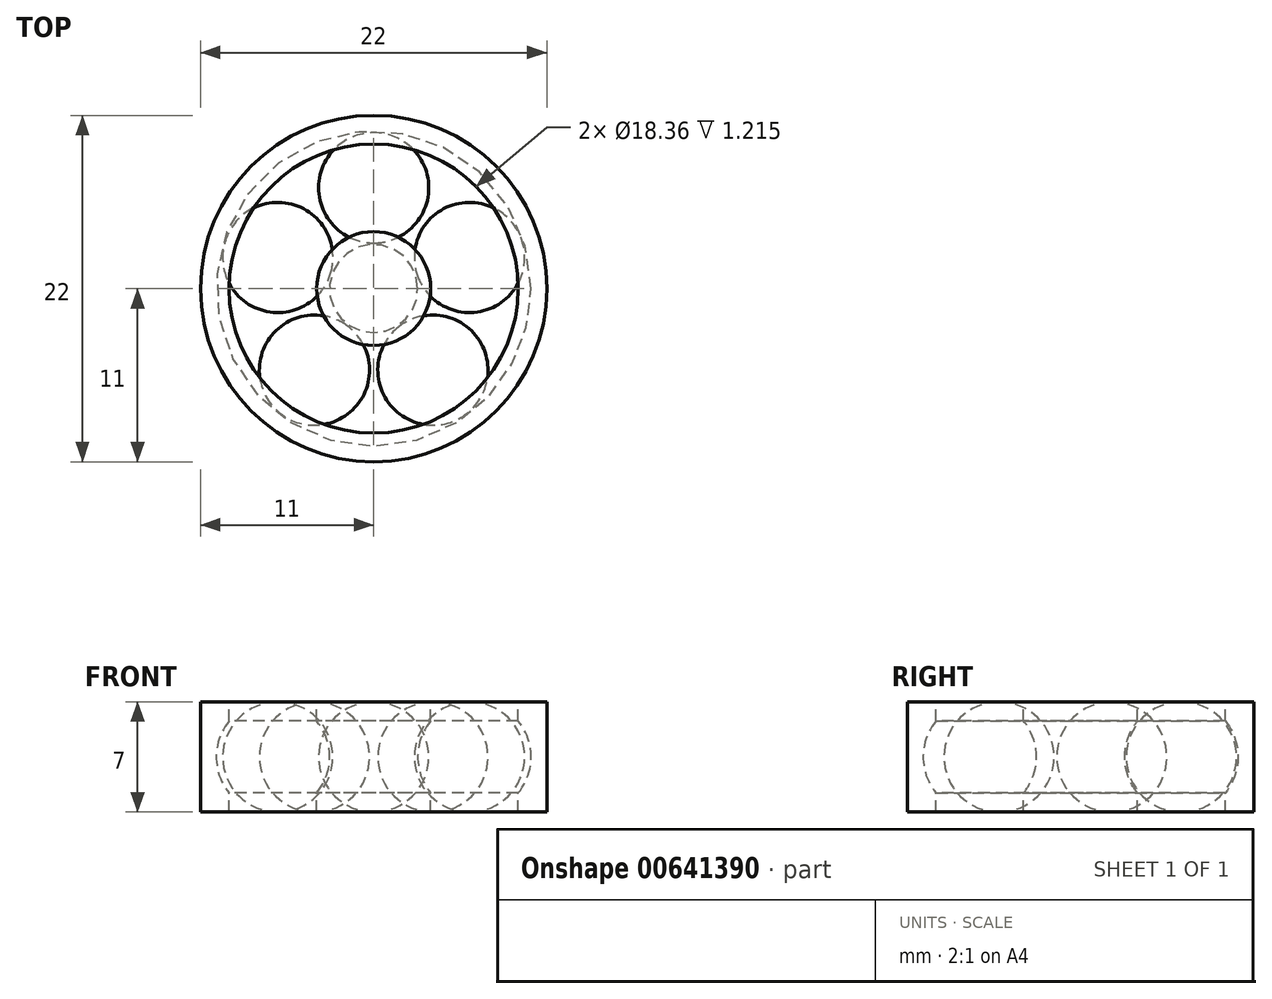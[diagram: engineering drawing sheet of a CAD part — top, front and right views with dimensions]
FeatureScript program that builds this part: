
annotation { "Feature Type Name" : "Feature", "Feature Type Description" : "" }
export const myFeature = defineFeature(function(context is Context, id is Id, definition is map)
    precondition{}
    {
        {
            var Q0;
            Q0=qCreatedBy(makeId("Right.planeOp"),FACE);
            var sketch = newSketch(context, id + "F0", { "sketchPlane" : qUnion([Q0])});
            skLineSegment(sketch, "E0", {"start": v(0, 3.5) * mm, "end": v(3.62, 3.5) * mm});
            skLineSegment(sketch, "E1", {"start": v(0, -3.5) * mm, "end": v(3.62, -3.5) * mm});
            skLineSegment(sketch, "E2", {"start": v(9.18, -3.5) * mm, "end": v(11, -3.5) * mm});
            skLineSegment(sketch, "E3", {"start": v(11, -3.5) * mm, "end": v(11, 3.5) * mm});
            skLineSegment(sketch, "E4", {"start": v(11, 3.5) * mm, "end": v(9.18, 3.5) * mm});
            skCircle(sketch, "E5", {"center": v(6.4, 0) * mm, "radius": 3.5 * mm});
            skLineSegment(sketch, "E6", {"start": v(9.18, 3.5) * mm, "end": v(3.62, 3.5) * mm, "construction": true});
            skLineSegment(sketch, "E7", {"start": v(3.62, -3.5) * mm, "end": v(3.62, 3.5) * mm, "construction": true});
            skLineSegment(sketch, "E8", {"start": v(3.62, -3.5) * mm, "end": v(9.18, -3.5) * mm, "construction": true});
            skLineSegment(sketch, "E9", {"start": v(9.18, 3.5) * mm, "end": v(9.18, -3.5) * mm, "construction": true});
            skLineSegment(sketch, "E10", {"start": v(9.18, 0) * mm, "end": v(3.62, 0) * mm, "construction": true});
            skLineSegment(sketch, "E11", {"start": v(0, 3.5) * mm, "end": v(0, -3.5) * mm});
            skLineSegment(sketch, "E12", {"start": v(3.62, 3.5) * mm, "end": v(3.62, 2.29) * mm});
            skLineSegment(sketch, "E13", {"start": v(3.62, -2.29) * mm, "end": v(3.62, -3.5) * mm});
            skLineSegment(sketch, "E14", {"start": v(9.18, -2.29) * mm, "end": v(9.18, -3.5) * mm});
            skLineSegment(sketch, "E15", {"start": v(9.18, 2.29) * mm, "end": v(9.18, 3.5) * mm});
            skArc(sketch, "E16", {"start": v(3.62, 2.29) * mm, "mid": v(2.8, 0) * mm, "end": v(3.62, -2.29) * mm});
            skArc(sketch, "E17", {"start": v(3.62, -2.29) * mm, "mid": v(6.4, -3.6) * mm, "end": v(9.18, -2.29) * mm, "construction": true});
            skArc(sketch, "E18", {"start": v(9.18, -2.29) * mm, "mid": v(10, 0) * mm, "end": v(9.18, 2.29) * mm});
            skArc(sketch, "E19", {"start": v(9.18, 2.29) * mm, "mid": v(6.4, 3.6) * mm, "end": v(3.62, 2.29) * mm, "construction": true});
            skLineSegment(sketch, "E20", {"start": v(0, 4.54) * mm, "end": v(0, -4.64) * mm, "construction": true});
            skLineSegment(sketch, "E21", {"start": v(6.4, -3.5) * mm, "end": v(6.4, 3.5) * mm});
            skSolve(sketch);
        }
        {
            var Q0;
            Q0=makeQuery(id+"F0.imprint","IMPRINT",FACE,{"disambiguationData":[TD([[makeQuery(id+"F0.imprint","IMPRINT",EDGE,{"derivedFrom":sQuery(id+"F0.wireOp",EDGE,"E0")}),-1.0]])]});
            var Q1;
            Q1=makeQuery(id+"F0.imprint","IMPRINT",FACE,{"disambiguationData":[TD([[makeQuery(id+"F0.imprint","IMPRINT",EDGE,{"derivedFrom":sQuery(id+"F0.wireOp",EDGE,"E2")}),1.0]])]});
            var Q2;
            Q2=sQuery(id+"F0.wireOp",EDGE,"E20");
            revolve(context, id + "F1", {"entities" : qUnion([Q0, Q1]), "axis" : qUnion([Q2]), "revolveType" : RevolveType.FULL});
        }
        {
            var Q0;
            {var subQ0=sQuery(id+"F0.wireOp",EDGE,"E21");Q0=makeQuery(id+"F0.imprint","IMPRINT",FACE,{"disambiguationData":[TD([[makeQuery(id+"F0.imprint","IMPRINT",EDGE,{"derivedFrom":subQ0}),-1.0]])]});}
            var Q1;
            Q1=sQuery(id+"F0.wireOp",EDGE,"E21");
            revolve(context, id + "F2", {"entities" : qUnion([Q0]), "axis" : qUnion([Q1]), "revolveType" : RevolveType.FULL});
        }
        {
            var Q0;
            Q0=makeQuery(id+"F2.opRevolve","SWEPT_BODY",BODY,{"disambiguationData":[OSD([sQuery(id+"F0.wireOp",EDGE,"E5"),sQuery(id+"F0.wireOp",EDGE,"E21")])]});
            var Q1;
            Q1=sQuery(id+"F0.wireOp",EDGE,"E11");
            circularPattern(context, id + "F3", {"entities" : qUnion([Q0]), "axis" : qUnion([Q1]), "angle" : 360 * degree, "instanceCount" : 5, "equalSpace" : true});
        }
    });
